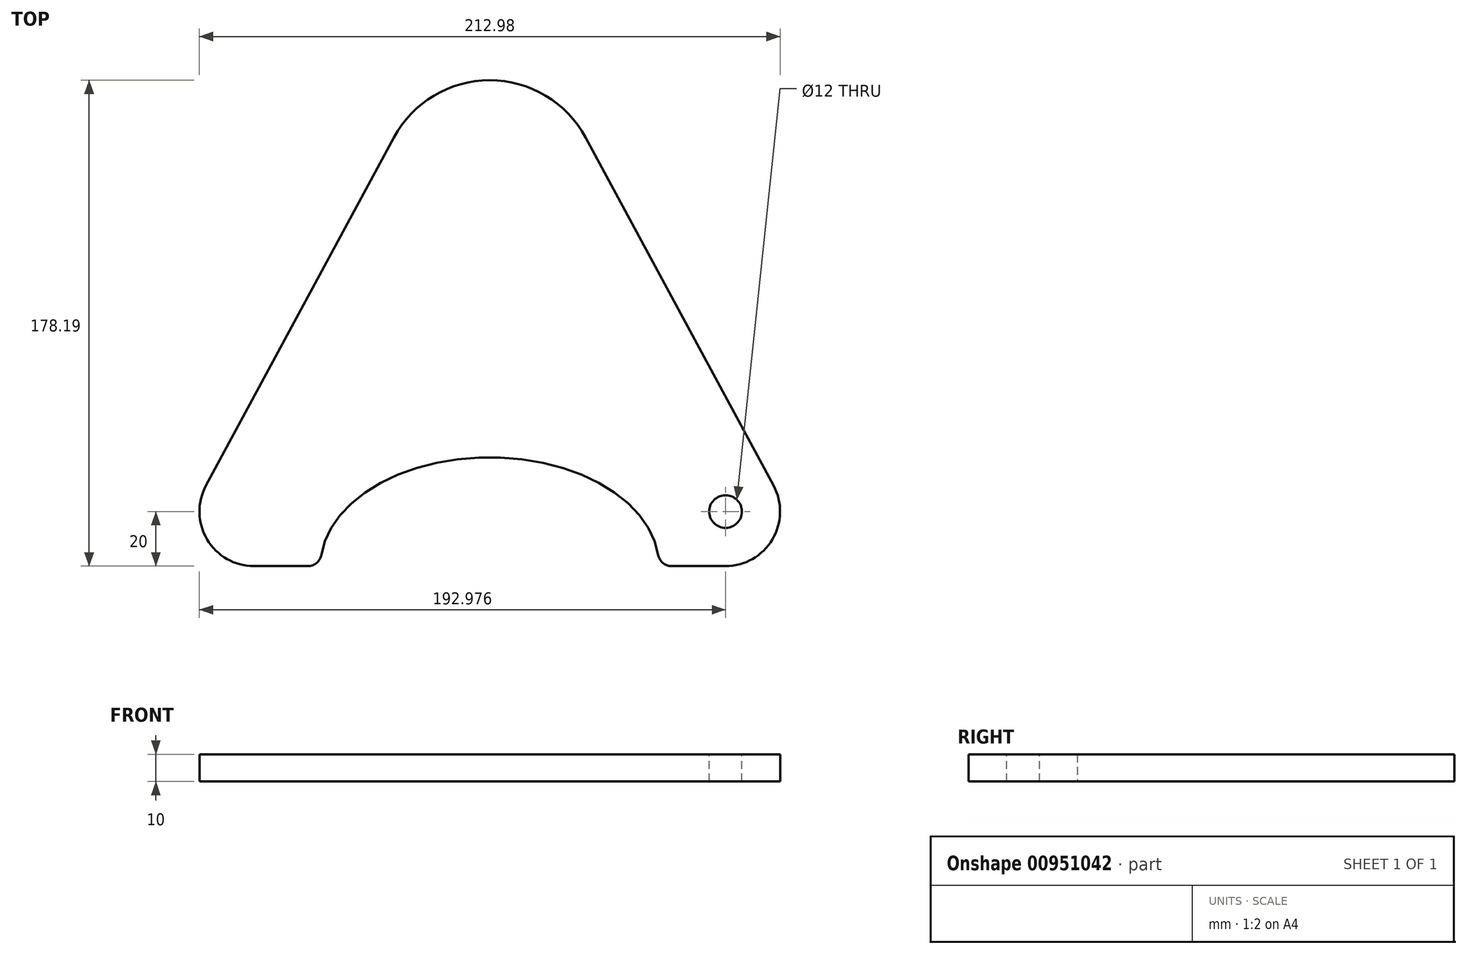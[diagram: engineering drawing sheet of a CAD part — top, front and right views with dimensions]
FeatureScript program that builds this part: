
annotation { "Feature Type Name" : "Feature", "Feature Type Description" : "" }
export const myFeature = defineFeature(function(context is Context, id is Id, definition is map)
    precondition{}
    {
        {
            var Q0;
            Q0=qCreatedBy(makeId("Top.planeOp"),FACE);
            var sketch = newSketch(context, id + "F0", { "sketchPlane" : qUnion([Q0])});
            skLineSegment(sketch, "E0", {"start": v(0, 0) * mm, "end": v(86.49, 0) * mm});
            skLineSegment(sketch, "E1", {"start": v(104.09, 29.5) * mm, "end": v(35.2, 157.18) * mm});
            skLineSegment(sketch, "E2.MirrorCS", {"start": v(-104.09, 29.5) * mm, "end": v(-35.2, 157.18) * mm});
            skLineSegment(sketch, "E3.MirrorCS", {"start": v(0, 0) * mm, "end": v(-86.49, 0) * mm});
            skPoint(sketch, "E4.visualSharp", {"position": v(0, 222.44) * mm});
            skArc(sketch, "E4.filletArc", {"start": v(35.2, 157.18) * mm, "mid": v(0, 178.2) * mm, "end": v(-35.2, 157.18) * mm});
            skPoint(sketch, "E5.visualSharp", {"position": v(-120, 0) * mm});
            skArc(sketch, "E5.filletArc", {"start": v(-104.09, 29.5) * mm, "mid": v(-103.66, 9.75) * mm, "end": v(-86.49, 0) * mm});
            skPoint(sketch, "E6.visualSharp", {"position": v(120, 0) * mm});
            skArc(sketch, "E6.filletArc", {"start": v(86.49, 0) * mm, "mid": v(103.66, 9.75) * mm, "end": v(104.09, 29.5) * mm});
            skSolve(sketch);
        }
        {
            var Q0;
            Q0 = qSketchRegion(id + "F0", true);
            extrude(context, id + "F1", {"entities" : qUnion([Q0]), "depth" : 10 * mm, "offsetDistance" : 25 * mm});
        }
        {
            var Q0;
            Q0=makeQuery(id+"F1.opExtrude","CAP_FACE",FACE,{"disambiguationData":[OSD([sQuery(id+"F0.wireOp",EDGE,"E0"),sQuery(id+"F0.wireOp",EDGE,"E1"),sQuery(id+"F0.wireOp",EDGE,"E2.MirrorCS"),sQuery(id+"F0.wireOp",EDGE,"E3.MirrorCS"),sQuery(id+"F0.wireOp",EDGE,"E4.filletArc"),sQuery(id+"F0.wireOp",EDGE,"E5.filletArc"),sQuery(id+"F0.wireOp",EDGE,"E6.filletArc")])],"isStart":false});
            var sketch = newSketch(context, id + "F2", { "sketchPlane" : qUnion([Q0])});
            skLineSegment(sketch, "E7", {"start": v(103.66, 9.75) * mm, "end": v(86.49, 20) * mm});
            skLineSegment(sketch, "E8", {"start": v(0, 0) * mm, "end": v(0, 73.33) * mm});
            skSolve(sketch);
        }
        {
            var Q0;
            Q0=sQuery(id+"F2.wireOp",VERTEX,"E7.end");
            var Q1;
            Q1=makeQuery(id+"F1.opExtrude","SWEPT_BODY",BODY,{"disambiguationData":[OSD([sQuery(id+"F0.wireOp",EDGE,"E0"),sQuery(id+"F0.wireOp",EDGE,"E1"),sQuery(id+"F0.wireOp",EDGE,"E2.MirrorCS"),sQuery(id+"F0.wireOp",EDGE,"E3.MirrorCS"),sQuery(id+"F0.wireOp",EDGE,"E4.filletArc"),sQuery(id+"F0.wireOp",EDGE,"E5.filletArc"),sQuery(id+"F0.wireOp",EDGE,"E6.filletArc")])]});
            hole(context, id + "F3", {"style" : HoleStyle.SIMPLE, "endStyle" : HoleEndStyle.THROUGH, "holeDiameter" : 12 * mm, "majorDiameter" : 5 * mm, "isTappedThrough" : true, "tappedDepth" : 12 * mm, "tapClearance" : 3, "startFromSketch" : true, "locations" : qUnion([Q0]), "scope" : qUnion([Q1])});
        }
        {
            var Q0;
            Q0=makeQuery(id+"F1.opExtrude","CAP_FACE",FACE,{"disambiguationData":[OSD([sQuery(id+"F0.wireOp",EDGE,"E0"),sQuery(id+"F0.wireOp",EDGE,"E1"),sQuery(id+"F0.wireOp",EDGE,"E2.MirrorCS"),sQuery(id+"F0.wireOp",EDGE,"E3.MirrorCS"),sQuery(id+"F0.wireOp",EDGE,"E4.filletArc"),sQuery(id+"F0.wireOp",EDGE,"E5.filletArc"),sQuery(id+"F0.wireOp",EDGE,"E6.filletArc")])],"isStart":false});
            var sketch = newSketch(context, id + "F4", { "sketchPlane" : qUnion([Q0])});
            skEllipse(sketch, "E9", {"center": v(0, 0) * mm, "majorRadius": 62.11 * mm, "minorRadius": 39.9 * mm, "majorAxis": v(1, 0)});
            skSolve(sketch);
        }
        {
            var Q0;
            Q0 = qSketchRegion(id + "F4", true);
            extrude(context, id + "F5", {"entities" : qUnion([Q0]), "operationType" : NewBodyOperationType.REMOVE, "oppositeDirection" : true, "depth" : 25 * mm, "offsetDistance" : 25 * mm});
        }
        {
            var Q0;
            Q0=makeQuery(id+"F5.boolean.opBoolean","INTERSECT",EDGE,{"disambiguationData":[OD(1.0)],"derivedFrom":[makeQuery(id+"F1.opExtrude","SWEPT_FACE",FACE,{"disambiguationData":[OSD([sQuery(id+"F0.wireOp",EDGE,"E0"),sQuery(id+"F0.wireOp",EDGE,"E3.MirrorCS")])]}),makeQuery(id+"F5.opExtrude","SWEPT_FACE",FACE,{"disambiguationData":[OSD([sQuery(id+"F4.wireOp",EDGE,"E9")])]})]});
            var Q1;
            Q1=makeQuery(id+"F5.boolean.opBoolean","INTERSECT",EDGE,{"disambiguationData":[OD(0.0)],"derivedFrom":[makeQuery(id+"F1.opExtrude","SWEPT_FACE",FACE,{"disambiguationData":[OSD([sQuery(id+"F0.wireOp",EDGE,"E0"),sQuery(id+"F0.wireOp",EDGE,"E3.MirrorCS")])]}),makeQuery(id+"F5.opExtrude","SWEPT_FACE",FACE,{"disambiguationData":[OSD([sQuery(id+"F4.wireOp",EDGE,"E9")])]})]});
            fillet(context, id + "F6", {"entities" : qUnion([Q0, Q1]), "tangentPropagation" : true, "radius" : 5 * mm, "defaultsChanged" : false, "vertexSettings" : [], "allowEdgeOverflow" : false});
        }
    });
